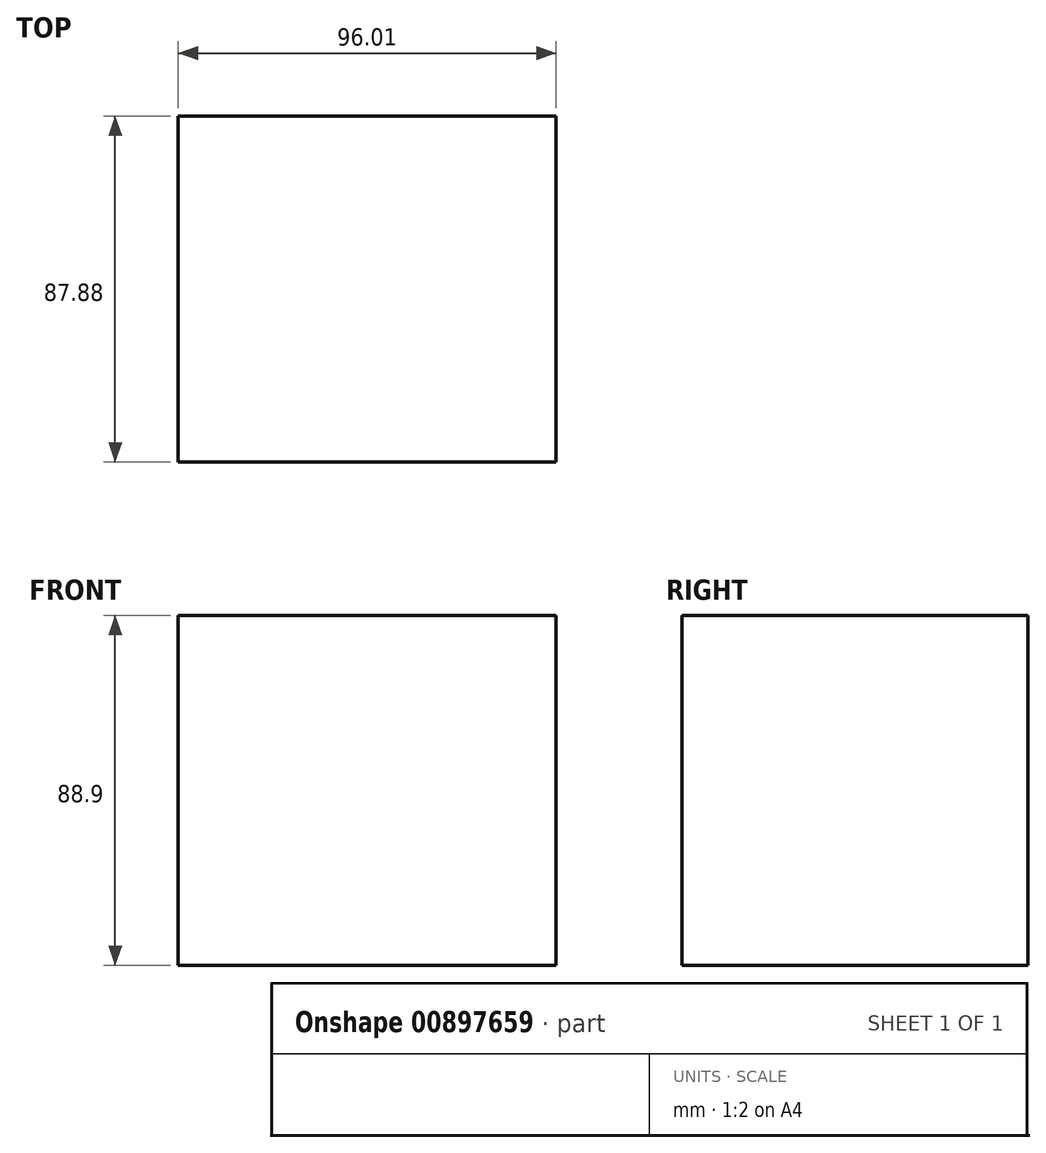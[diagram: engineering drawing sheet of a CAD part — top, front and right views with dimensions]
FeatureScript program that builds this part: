
annotation { "Feature Type Name" : "Feature", "Feature Type Description" : "" }
export const myFeature = defineFeature(function(context is Context, id is Id, definition is map)
    precondition{}
    {
        {
            var Q0;
            Q0=qCreatedBy(makeId("Front.planeOp"),FACE);
            var sketch = newSketch(context, id + "F0", { "sketchPlane" : qUnion([Q0])});
            skLineSegment(sketch, "E0", {"start": v(-50.45, 41.86) * mm, "end": v(-50.45, -47.04) * mm});
            skLineSegment(sketch, "E1", {"start": v(-50.45, 41.86) * mm, "end": v(45.56, 41.86) * mm});
            skLineSegment(sketch, "E2", {"start": v(45.56, 41.86) * mm, "end": v(45.56, -47.04) * mm});
            skLineSegment(sketch, "E3", {"start": v(45.56, -47.04) * mm, "end": v(-50.45, -47.04) * mm});
            skSolve(sketch);
        }
        {
            var Q0;
            Q0 = qSketchRegion(id + "F0", true);
            extrude(context, id + "F1", {"entities" : qUnion([Q0]), "depth" : 87.88 * mm, "offsetDistance" : 25.4 * mm});
        }
    });
